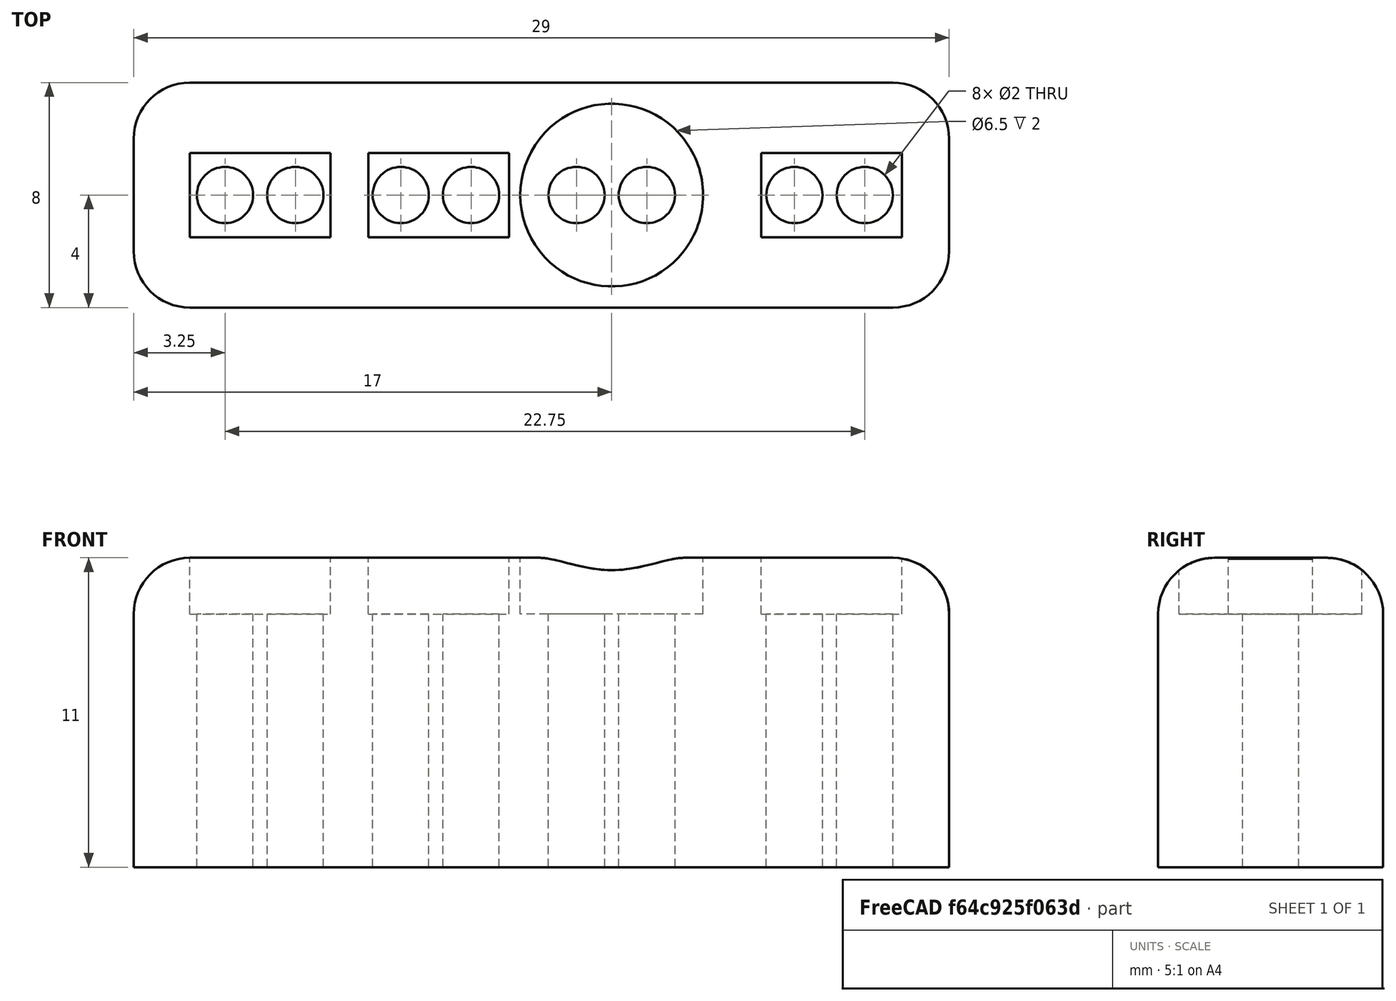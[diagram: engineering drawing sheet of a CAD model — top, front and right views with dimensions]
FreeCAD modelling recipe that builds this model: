
FCSTD DOCUMENT  (FreeCAD 0.19R24276 (Git))
Label: standoff2
License: All rights reserved
LicenseURL: http://en.wikipedia.org/wiki/All_rights_reserved
objects: Part::Cylinder×9, Part::MultiFuse×5, Part::Box×4, Part::Fillet×1, Part::Cut×1
note: 20 computed .brp shape members not serialized (recipe doc carries the construction recipe); baked Part::Feature solids carry a one-line shape summary decoded from their .brp

FEATURE [Part::Box] Box  label="Cube"
  AttacherType = Attacher::AttachEngine3D
  Height = 11
  Length = 29
  Placement = pos=(0,-1,0) rot=(0,0,1;0rad)
  Width = 8
FEATURE [Part::Box] Box001  label="Cube001"
  AttacherType = Attacher::AttachEngine3D
  Height = 10
  Length = 5
  Placement = pos=(2,1.5,9) rot=(0,0,1;0rad)
  Width = 3
FEATURE [Part::Box] Box002  label="Cube002"
  AttacherType = Attacher::AttachEngine3D
  Height = 10
  Length = 5
  Placement = pos=(8.35,1.5,9) rot=(0,0,1;0rad)
  Width = 3
FEATURE [Part::Box] Box003  label="Cube003"
  AttacherType = Attacher::AttachEngine3D
  Height = 10
  Length = 5
  Placement = pos=(22.32,1.5,9) rot=(0,0,1;0rad)
  Width = 3
FEATURE [Part::Cylinder] Cylinder
  Angle = 360
  AttacherType = Attacher::AttachEngine3D
  Height = 10
  Placement = pos=(17,3,9) rot=(0,0,1;0rad)
  Radius = 3.25
FEATURE [Part::Cylinder] Cylinder001
  Angle = 360
  AttacherType = Attacher::AttachEngine3D
  Height = 20
  Placement = pos=(3.25,3,0) rot=(0,0,1;0rad)
  Radius = 1
FEATURE [Part::Cylinder] Cylinder002
  Angle = 360
  AttacherType = Attacher::AttachEngine3D
  Height = 20
  Placement = pos=(5.75,3,0) rot=(0,0,1;0rad)
  Radius = 1
FEATURE [Part::MultiFuse] Fusion
  Shapes = -> [Cylinder001,Cylinder002]
FEATURE [Part::Cylinder] Cylinder003
  Angle = 360
  AttacherType = Attacher::AttachEngine3D
  Height = 20
  Placement = pos=(3.25,3,0) rot=(0,0,1;0rad)
  Radius = 1
FEATURE [Part::Cylinder] Cylinder004
  Angle = 360
  AttacherType = Attacher::AttachEngine3D
  Height = 20
  Placement = pos=(5.75,3,0) rot=(0,0,1;0rad)
  Radius = 1
FEATURE [Part::MultiFuse] Fusion001
  Placement = pos=(6.25,0,0) rot=(0,0,1;0rad)
  Shapes = -> [Cylinder003,Cylinder004]
FEATURE [Part::Cylinder] Cylinder005
  Angle = 360
  AttacherType = Attacher::AttachEngine3D
  Height = 20
  Placement = pos=(3.25,3,0) rot=(0,0,1;0rad)
  Radius = 1
FEATURE [Part::Cylinder] Cylinder006
  Angle = 360
  AttacherType = Attacher::AttachEngine3D
  Height = 20
  Placement = pos=(5.75,3,0) rot=(0,0,1;0rad)
  Radius = 1
FEATURE [Part::MultiFuse] Fusion002
  Placement = pos=(20.25,0,0) rot=(0,0,1;0rad)
  Shapes = -> [Cylinder005,Cylinder006]
FEATURE [Part::Cylinder] Cylinder007
  Angle = 360
  AttacherType = Attacher::AttachEngine3D
  Height = 20
  Placement = pos=(3.25,3,0) rot=(0,0,1;0rad)
  Radius = 1
FEATURE [Part::Cylinder] Cylinder008
  Angle = 360
  AttacherType = Attacher::AttachEngine3D
  Height = 20
  Placement = pos=(5.75,3,0) rot=(0,0,1;0rad)
  Radius = 1
FEATURE [Part::MultiFuse] Fusion003
  Placement = pos=(12.5,0,0) rot=(0,0,1;0rad)
  Shapes = -> [Cylinder007,Cylinder008]
FEATURE [Part::Fillet] Fillet
  Base = -> Box
  Edges = 8 edges r=2: [Edge1,Edge2,Edge3,Edge5,Edge6,Edge7,Edge10,Edge12]
FEATURE [Part::MultiFuse] Fusion004
  Shapes = -> [Fusion003,Box001,Box002,Box003,Cylinder,Fusion,Fusion001,Fusion002]
FEATURE [Part::Cut] Cut  label="standoff"
  Base = -> Fillet
  Tool = -> Fusion004
